# Revit family: Table-Teknion-PCMT_Mitis-R2015
name_source: partatom
category: Furniture
revit_build: Autodesk Revit Architecture 2016 (Build: 20190507_1515(x64)
units: mm (PartAtom-declared; Revit-internal decimal feet)

## family parameters
Always vertical = Yes
Cut with Voids When Loaded = No
OmniClass Number = 23.40.20.00
OmniClass Title = General Furniture and Specialties
Room Calculation Point = No
Shared = Yes
Work Plane-Based = No

## types (2) — shared parameters
Assembly Code = E2020200
Manufacturer = Teknion
Manufacturer Fax = 416.661.4586
Part Number = PCMT
Product Documentation Link = https://d2r72yk5wmppdj.cloudfront.net
Product Line = Punt Collection
Product Page URL = https://www.teknion.com
Series = Punt Collection
Sustainability Data = http://www.teknion.com
URL = www.teknion.com
Unit Weight URL = http://www.teknion.com
Warranty = http://www.teknion.com

## per-type parameters (varying)
| type | Description | Glass Top | Model | Wood Top |
| Punt Wood Table Finish | Punt Collection, Mitis Table - Punt Wood Surface Finish | No | PCMT_______PW | Yes |
| Punt Glass Table Finish | Punt Collection, Mitis Table - Punt Glass Surface Finish | Yes | PCMT_______PG | No |

## geometry (parser evidence)
native form markers: Sweep x2
no freeform markers — native parametric forms only
